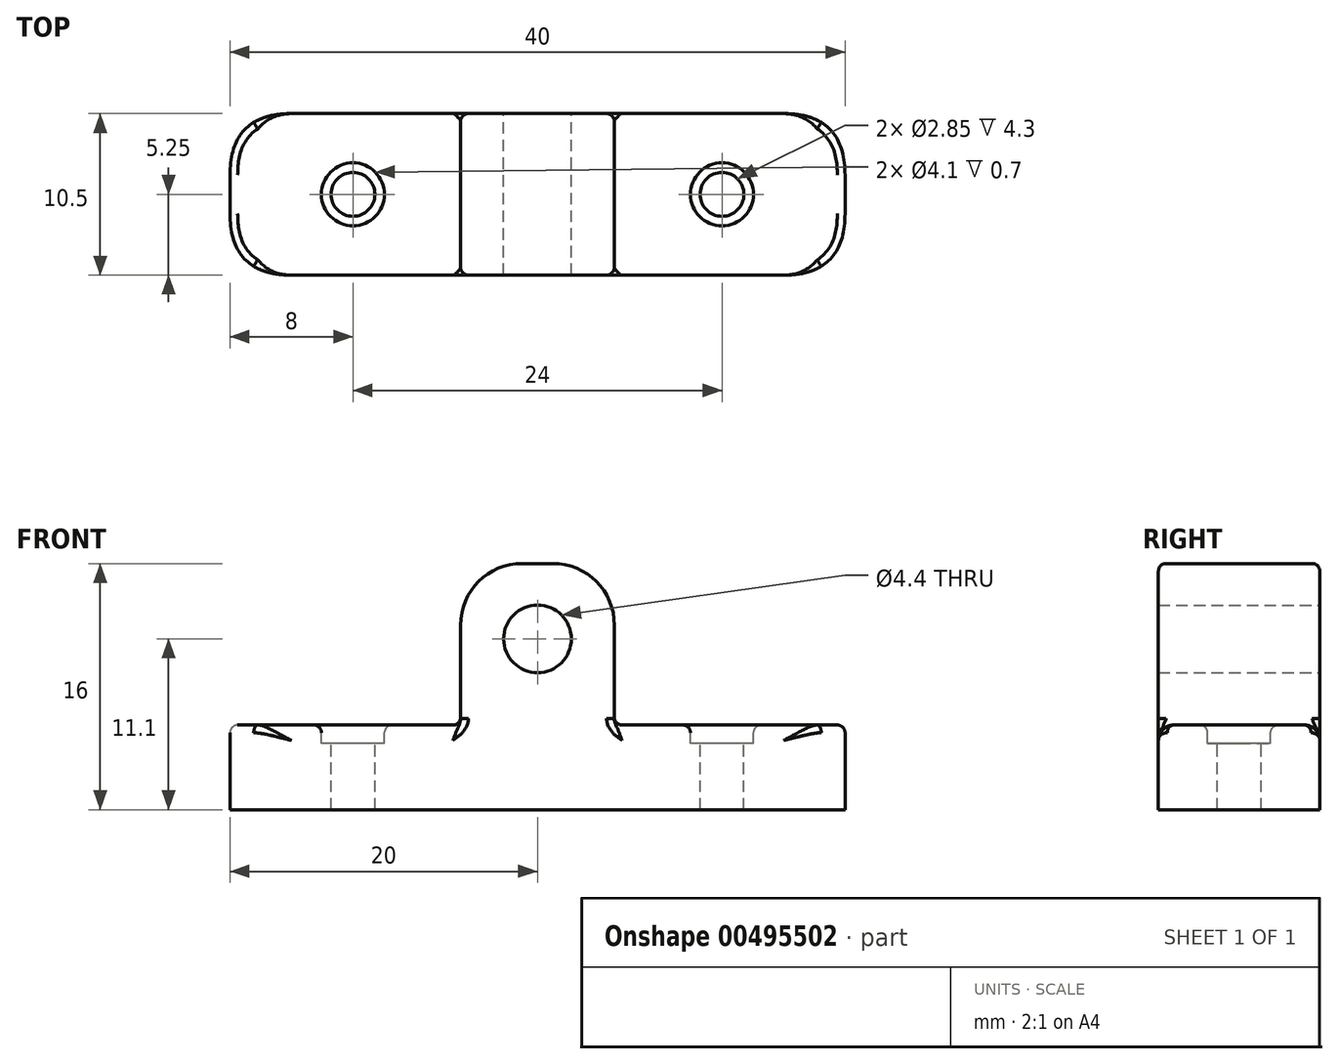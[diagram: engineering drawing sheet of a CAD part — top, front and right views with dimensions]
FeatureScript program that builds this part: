
annotation { "Feature Type Name" : "Feature", "Feature Type Description" : "" }
export const myFeature = defineFeature(function(context is Context, id is Id, definition is map)
    precondition{}
    {
        {
            var Q0;
            Q0=qCreatedBy(makeId("Front.planeOp"),FACE);
            var sketch = newSketch(context, id + "F0", { "sketchPlane" : qUnion([Q0])});
            skLineSegment(sketch, "E0.bottom", {"start": v(-20, 2.75) * mm, "end": v(20, 2.75) * mm});
            skLineSegment(sketch, "E0.top", {"start": v(-20, -2.75) * mm, "end": v(20, -2.75) * mm});
            skLineSegment(sketch, "E0.left", {"start": v(-20, 2.75) * mm, "end": v(-20, -2.75) * mm});
            skLineSegment(sketch, "E0.right", {"start": v(20, 2.75) * mm, "end": v(20, -2.75) * mm});
            skPoint(sketch, "E0.middle", {"position": v(0, 0) * mm});
            skLineSegment(sketch, "E1.top", {"start": v(0, 13.25) * mm, "end": v(5, 13.25) * mm});
            skLineSegment(sketch, "E1.right", {"start": v(5, 2.75) * mm, "end": v(5, 13.25) * mm});
            skLineSegment(sketch, "E2.MirrorCS", {"start": v(0, 13.25) * mm, "end": v(-5, 13.25) * mm});
            skLineSegment(sketch, "E3.MirrorCS", {"start": v(-5, 2.75) * mm, "end": v(-5, 13.25) * mm});
            skCircle(sketch, "E4", {"center": v(0, 8.35) * mm, "radius": 2.2 * mm});
            skSolve(sketch);
        }
        {
            var Q0;
            Q0=makeQuery(id+"F0.imprint","IMPRINT",FACE,{"disambiguationData":[TD([[makeQuery(id+"F0.imprint","IMPRINT",EDGE,{"derivedFrom":sQuery(id+"F0.wireOp",EDGE,"E1.top")}),-1.0]])]});
            var Q1;
            Q1=makeQuery(id+"F0.imprint","IMPRINT",FACE,{"disambiguationData":[TD([[makeQuery(id+"F0.imprint","IMPRINT",EDGE,{"derivedFrom":sQuery(id+"F0.wireOp",EDGE,"E0.top")}),1.0]])]});
            extrude(context, id + "F1", {"entities" : qUnion([Q0, Q1]), "depth" : 10.5 * mm});
        }
        {
            var Q0;
            Q0=makeQuery(id+"F1.opExtrude","SWEPT_EDGE",EDGE,{"disambiguationData":[OSD([sQuery(id+"F0.wireOp",EDGE,"E2.MirrorCS"),sQuery(id+"F0.wireOp",EDGE,"E3.MirrorCS")])]});
            var Q1;
            Q1=makeQuery(id+"F1.opExtrude","SWEPT_EDGE",EDGE,{"disambiguationData":[OSD([sQuery(id+"F0.wireOp",EDGE,"E1.top"),sQuery(id+"F0.wireOp",EDGE,"E1.right")])]});
            fillet(context, id + "F2", {"entities" : qUnion([Q0, Q1]), "radius" : 4 * mm, "tangentPropagation" : true, "allowEdgeOverflow" : false});
        }
        {
            var Q0;
            {var subQ0=sQuery(id+"F0.wireOp",EDGE,"E0.bottom");Q0=makeQuery(id+"F1.opExtrude","SWEPT_FACE",FACE,{"disambiguationData":[OSD([subQ0]),TDD([makeQuery(id+"F0.imprint","IMPRINT",EDGE,{"disambiguationData":[TD([[makeQuery(id+"F0.imprint","INTERSECT",VERTEX,{"derivedFrom":[subQ0,sQuery(id+"F0.wireOp",EDGE,"E0.left")]}),-1.0]])],"derivedFrom":subQ0})])]});}
            var sketch = newSketch(context, id + "F3", { "sketchPlane" : qUnion([Q0])});
            skPoint(sketch, "E5", {"position": v(-12, -5.25) * mm});
            skLineSegment(sketch, "E6", {"start": v(-5, -5.25) * mm, "end": v(-20, -5.25) * mm});
            skPoint(sketch, "E7.MirrorP", {"position": v(12, -5.25) * mm});
            skSolve(sketch);
        }
        {
            var Q0;
            Q0=sQuery(id+"F3.wireOp",VERTEX,"E5");
            var Q1;
            Q1=makeQuery(id+"F1.opExtrude","SWEPT_BODY",BODY,{"disambiguationData":[OSD([sQuery(id+"F0.wireOp",EDGE,"E0.bottom"),sQuery(id+"F0.wireOp",EDGE,"E0.top"),sQuery(id+"F0.wireOp",EDGE,"E0.left"),sQuery(id+"F0.wireOp",EDGE,"E0.right"),sQuery(id+"F0.wireOp",EDGE,"E1.top"),sQuery(id+"F0.wireOp",EDGE,"E1.right"),sQuery(id+"F0.wireOp",EDGE,"E2.MirrorCS"),sQuery(id+"F0.wireOp",EDGE,"E3.MirrorCS"),sQuery(id+"F0.wireOp",EDGE,"E4")])]});
            hole(context, id + "F4", {"style" : HoleStyle.C_BORE, "endStyle" : HoleEndStyle.THROUGH, "holeDiameter" : 2.85 * mm, "cBoreDiameter" : 4.1 * mm, "cBoreDepth" : 1.2 * mm, "isTappedThrough" : true, "tappedDepth" : 12 * mm, "tapClearance" : 3, "locations" : qUnion([Q0]), "scope" : qUnion([Q1])});
        }
        {
            var Q0;
            Q0=sQuery(id+"F3.wireOp",VERTEX,"E7.MirrorP");
            var Q1;
            Q1=makeQuery(id+"F1.opExtrude","SWEPT_BODY",BODY,{"disambiguationData":[OSD([sQuery(id+"F0.wireOp",EDGE,"E0.bottom"),sQuery(id+"F0.wireOp",EDGE,"E0.top"),sQuery(id+"F0.wireOp",EDGE,"E0.left"),sQuery(id+"F0.wireOp",EDGE,"E0.right"),sQuery(id+"F0.wireOp",EDGE,"E1.top"),sQuery(id+"F0.wireOp",EDGE,"E1.right"),sQuery(id+"F0.wireOp",EDGE,"E2.MirrorCS"),sQuery(id+"F0.wireOp",EDGE,"E3.MirrorCS"),sQuery(id+"F0.wireOp",EDGE,"E4")])]});
            hole(context, id + "F5", {"style" : HoleStyle.C_BORE, "endStyle" : HoleEndStyle.THROUGH, "holeDiameter" : 2.85 * mm, "cBoreDiameter" : 4.1 * mm, "cBoreDepth" : 1.2 * mm, "isTappedThrough" : true, "tappedDepth" : 12 * mm, "tapClearance" : 3, "locations" : qUnion([Q0]), "scope" : qUnion([Q1])});
        }
        {
            var Q0;
            {var subQ0=sQuery(id+"F0.wireOp",EDGE,"E0.bottom");Q0=makeQuery(id+"F1.opExtrude","CAP_EDGE",EDGE,{"disambiguationData":[OSD([subQ0]),TDD([makeQuery(id+"F0.imprint","IMPRINT",EDGE,{"disambiguationData":[TD([[makeQuery(id+"F0.imprint","INTERSECT",VERTEX,{"derivedFrom":[subQ0,sQuery(id+"F0.wireOp",EDGE,"E0.right")]}),1.0]])],"derivedFrom":subQ0})])],"isStart":true});}
            var Q1;
            {var subQ0=sQuery(id+"F0.wireOp",EDGE,"E0.bottom");Q1=makeQuery(id+"F1.opExtrude","CAP_EDGE",EDGE,{"disambiguationData":[OSD([subQ0]),TDD([makeQuery(id+"F0.imprint","IMPRINT",EDGE,{"disambiguationData":[TD([[makeQuery(id+"F0.imprint","INTERSECT",VERTEX,{"derivedFrom":[subQ0,sQuery(id+"F0.wireOp",EDGE,"E0.right")]}),1.0]])],"derivedFrom":subQ0})])],"isStart":false});}
            var Q2;
            {var subQ0=sQuery(id+"F0.wireOp",EDGE,"E0.bottom");Q2=makeQuery(id+"F1.opExtrude","CAP_EDGE",EDGE,{"disambiguationData":[OSD([subQ0]),TDD([makeQuery(id+"F0.imprint","IMPRINT",EDGE,{"disambiguationData":[TD([[makeQuery(id+"F0.imprint","INTERSECT",VERTEX,{"derivedFrom":[subQ0,sQuery(id+"F0.wireOp",EDGE,"E0.left")]}),-1.0]])],"derivedFrom":subQ0})])],"isStart":false});}
            var Q3;
            {var subQ0=sQuery(id+"F0.wireOp",EDGE,"E0.bottom");Q3=makeQuery(id+"F1.opExtrude","CAP_EDGE",EDGE,{"disambiguationData":[OSD([subQ0]),TDD([makeQuery(id+"F0.imprint","IMPRINT",EDGE,{"disambiguationData":[TD([[makeQuery(id+"F0.imprint","INTERSECT",VERTEX,{"derivedFrom":[subQ0,sQuery(id+"F0.wireOp",EDGE,"E0.left")]}),-1.0]])],"derivedFrom":subQ0})])],"isStart":true});}
            fillet(context, id + "F6", {"entities" : qUnion([Q0, Q1, Q2, Q3]), "radius" : 1 * mm, "tangentPropagation" : true, "allowEdgeOverflow" : false});
        }
        {
            var Q0;
            Q0=makeQuery(id+"F1.opExtrude","CAP_EDGE",EDGE,{"disambiguationData":[OSD([sQuery(id+"F0.wireOp",EDGE,"E0.right")])],"isStart":false});
            var Q1;
            Q1=makeQuery(id+"F1.opExtrude","CAP_EDGE",EDGE,{"disambiguationData":[OSD([sQuery(id+"F0.wireOp",EDGE,"E0.right")])],"isStart":true});
            fillet(context, id + "F7", {"entities" : qUnion([Q0, Q1]), "radius" : 4 * mm, "rho" : 0.5, "crossSection" : FilletCrossSection.CONIC, "allowEdgeOverflow" : false});
        }
        {
            var Q0;
            Q0=makeQuery(id+"F1.opExtrude","CAP_EDGE",EDGE,{"disambiguationData":[OSD([sQuery(id+"F0.wireOp",EDGE,"E0.left")])],"isStart":false});
            var Q1;
            Q1=makeQuery(id+"F1.opExtrude","CAP_EDGE",EDGE,{"disambiguationData":[OSD([sQuery(id+"F0.wireOp",EDGE,"E0.left")])],"isStart":true});
            fillet(context, id + "F8", {"entities" : qUnion([Q0, Q1]), "radius" : 4 * mm, "rho" : 0.5, "crossSection" : FilletCrossSection.CONIC, "allowEdgeOverflow" : false});
        }
        {
            var Q0;
            {var subQ0=sQuery(id+"F0.wireOp",EDGE,"E0.bottom");Q0=makeQuery(id+"F1.opExtrude","SWEPT_FACE",FACE,{"disambiguationData":[OSD([subQ0]),TDD([makeQuery(id+"F0.imprint","IMPRINT",EDGE,{"disambiguationData":[TD([[makeQuery(id+"F0.imprint","INTERSECT",VERTEX,{"derivedFrom":[subQ0,sQuery(id+"F0.wireOp",EDGE,"E0.right")]}),1.0]])],"derivedFrom":subQ0})])]});}
            fillet(context, id + "F9", {"entities" : qUnion([Q0]), "radius" : .5 * mm, "tangentPropagation" : true, "allowEdgeOverflow" : false});
        }
        {
            var Q0;
            Q0=makeQuery(id+"F1.opExtrude","SWEPT_EDGE",EDGE,{"disambiguationData":[OSD([sQuery(id+"F0.wireOp",EDGE,"E0.bottom"),sQuery(id+"F0.wireOp",EDGE,"E0.left")])]});
            var Q1;
            {var subQ0=sQuery(id+"F0.wireOp",EDGE,"E0.bottom");Q1=makeQuery(id+"F1.opExtrude","SWEPT_FACE",FACE,{"disambiguationData":[OSD([subQ0]),TDD([makeQuery(id+"F0.imprint","IMPRINT",EDGE,{"disambiguationData":[TD([[makeQuery(id+"F0.imprint","INTERSECT",VERTEX,{"derivedFrom":[subQ0,sQuery(id+"F0.wireOp",EDGE,"E0.left")]}),-1.0]])],"derivedFrom":subQ0})])]});}
            fillet(context, id + "F10", {"entities" : qUnion([Q0, Q1]), "radius" : .5 * mm, "tangentPropagation" : true, "allowEdgeOverflow" : false});
        }
        {
            var Q0;
            Q0=makeQuery(id+"F1.opExtrude","CAP_EDGE",EDGE,{"disambiguationData":[OSD([sQuery(id+"F0.wireOp",EDGE,"E3.MirrorCS")])],"isStart":false});
            var Q1;
            {var subQ0=sQuery(id+"F0.wireOp",EDGE,"E3.MirrorCS");var subQ1=sQuery(id+"F0.wireOp",EDGE,"E2.MirrorCS");Q1=makeQuery(id+"F2.opFillet","BLEND_EDGE",EDGE,{"blendedFrom":[makeQuery(id+"F1.opExtrude","SWEPT_EDGE",EDGE,{"disambiguationData":[OSD([subQ1,subQ0])]}),makeQuery(id+"F1.opExtrude","CAP_FACE",FACE,{"disambiguationData":[OSD([sQuery(id+"F0.wireOp",EDGE,"E0.bottom"),sQuery(id+"F0.wireOp",EDGE,"E0.top"),sQuery(id+"F0.wireOp",EDGE,"E0.left"),sQuery(id+"F0.wireOp",EDGE,"E0.right"),sQuery(id+"F0.wireOp",EDGE,"E1.top"),sQuery(id+"F0.wireOp",EDGE,"E1.right"),subQ1,subQ0,sQuery(id+"F0.wireOp",EDGE,"E4")])],"isStart":false})],"blendedInto":[makeQuery(id+"F1.opExtrude","CAP_FACE",FACE,{"disambiguationData":[OSD([sQuery(id+"F0.wireOp",EDGE,"E0.bottom"),sQuery(id+"F0.wireOp",EDGE,"E0.top"),sQuery(id+"F0.wireOp",EDGE,"E0.left"),sQuery(id+"F0.wireOp",EDGE,"E0.right"),sQuery(id+"F0.wireOp",EDGE,"E1.top"),sQuery(id+"F0.wireOp",EDGE,"E1.right"),subQ1,subQ0,sQuery(id+"F0.wireOp",EDGE,"E4")])],"isStart":false})]});}
            var Q2;
            Q2=makeQuery(id+"F1.opExtrude","CAP_EDGE",EDGE,{"disambiguationData":[OSD([sQuery(id+"F0.wireOp",EDGE,"E1.top"),sQuery(id+"F0.wireOp",EDGE,"E2.MirrorCS")])],"isStart":false});
            var Q3;
            {var subQ0=sQuery(id+"F0.wireOp",EDGE,"E1.right");var subQ1=sQuery(id+"F0.wireOp",EDGE,"E1.top");Q3=makeQuery(id+"F2.opFillet","BLEND_EDGE",EDGE,{"blendedFrom":[makeQuery(id+"F1.opExtrude","SWEPT_EDGE",EDGE,{"disambiguationData":[OSD([subQ1,subQ0])]}),makeQuery(id+"F1.opExtrude","CAP_FACE",FACE,{"disambiguationData":[OSD([sQuery(id+"F0.wireOp",EDGE,"E0.bottom"),sQuery(id+"F0.wireOp",EDGE,"E0.top"),sQuery(id+"F0.wireOp",EDGE,"E0.left"),sQuery(id+"F0.wireOp",EDGE,"E0.right"),subQ1,subQ0,sQuery(id+"F0.wireOp",EDGE,"E2.MirrorCS"),sQuery(id+"F0.wireOp",EDGE,"E3.MirrorCS"),sQuery(id+"F0.wireOp",EDGE,"E4")])],"isStart":false})],"blendedInto":[makeQuery(id+"F1.opExtrude","CAP_FACE",FACE,{"disambiguationData":[OSD([sQuery(id+"F0.wireOp",EDGE,"E0.bottom"),sQuery(id+"F0.wireOp",EDGE,"E0.top"),sQuery(id+"F0.wireOp",EDGE,"E0.left"),sQuery(id+"F0.wireOp",EDGE,"E0.right"),subQ1,subQ0,sQuery(id+"F0.wireOp",EDGE,"E2.MirrorCS"),sQuery(id+"F0.wireOp",EDGE,"E3.MirrorCS"),sQuery(id+"F0.wireOp",EDGE,"E4")])],"isStart":false})]});}
            var Q4;
            Q4=makeQuery(id+"F1.opExtrude","CAP_EDGE",EDGE,{"disambiguationData":[OSD([sQuery(id+"F0.wireOp",EDGE,"E1.right")])],"isStart":false});
            fillet(context, id + "F11", {"entities" : qUnion([Q0, Q1, Q2, Q3, Q4]), "radius" : .5 * mm, "tangentPropagation" : true, "allowEdgeOverflow" : false});
        }
        {
            var Q0;
            Q0=makeQuery(id+"F1.opExtrude","CAP_EDGE",EDGE,{"disambiguationData":[OSD([sQuery(id+"F0.wireOp",EDGE,"E1.right")])],"isStart":true});
            var Q1;
            {var subQ0=sQuery(id+"F0.wireOp",EDGE,"E1.right");var subQ1=sQuery(id+"F0.wireOp",EDGE,"E1.top");Q1=makeQuery(id+"F2.opFillet","BLEND_EDGE",EDGE,{"blendedFrom":[makeQuery(id+"F1.opExtrude","SWEPT_EDGE",EDGE,{"disambiguationData":[OSD([subQ1,subQ0])]}),makeQuery(id+"F1.opExtrude","CAP_FACE",FACE,{"disambiguationData":[OSD([sQuery(id+"F0.wireOp",EDGE,"E0.bottom"),sQuery(id+"F0.wireOp",EDGE,"E0.top"),sQuery(id+"F0.wireOp",EDGE,"E0.left"),sQuery(id+"F0.wireOp",EDGE,"E0.right"),subQ1,subQ0,sQuery(id+"F0.wireOp",EDGE,"E2.MirrorCS"),sQuery(id+"F0.wireOp",EDGE,"E3.MirrorCS"),sQuery(id+"F0.wireOp",EDGE,"E4")])],"isStart":true})],"blendedInto":[makeQuery(id+"F1.opExtrude","CAP_FACE",FACE,{"disambiguationData":[OSD([sQuery(id+"F0.wireOp",EDGE,"E0.bottom"),sQuery(id+"F0.wireOp",EDGE,"E0.top"),sQuery(id+"F0.wireOp",EDGE,"E0.left"),sQuery(id+"F0.wireOp",EDGE,"E0.right"),subQ1,subQ0,sQuery(id+"F0.wireOp",EDGE,"E2.MirrorCS"),sQuery(id+"F0.wireOp",EDGE,"E3.MirrorCS"),sQuery(id+"F0.wireOp",EDGE,"E4")])],"isStart":true})]});}
            var Q2;
            Q2=makeQuery(id+"F1.opExtrude","CAP_EDGE",EDGE,{"disambiguationData":[OSD([sQuery(id+"F0.wireOp",EDGE,"E1.top"),sQuery(id+"F0.wireOp",EDGE,"E2.MirrorCS")])],"isStart":true});
            var Q3;
            {var subQ0=sQuery(id+"F0.wireOp",EDGE,"E3.MirrorCS");var subQ1=sQuery(id+"F0.wireOp",EDGE,"E2.MirrorCS");Q3=makeQuery(id+"F2.opFillet","BLEND_EDGE",EDGE,{"blendedFrom":[makeQuery(id+"F1.opExtrude","SWEPT_EDGE",EDGE,{"disambiguationData":[OSD([subQ1,subQ0])]}),makeQuery(id+"F1.opExtrude","CAP_FACE",FACE,{"disambiguationData":[OSD([sQuery(id+"F0.wireOp",EDGE,"E0.bottom"),sQuery(id+"F0.wireOp",EDGE,"E0.top"),sQuery(id+"F0.wireOp",EDGE,"E0.left"),sQuery(id+"F0.wireOp",EDGE,"E0.right"),sQuery(id+"F0.wireOp",EDGE,"E1.top"),sQuery(id+"F0.wireOp",EDGE,"E1.right"),subQ1,subQ0,sQuery(id+"F0.wireOp",EDGE,"E4")])],"isStart":true})],"blendedInto":[makeQuery(id+"F1.opExtrude","CAP_FACE",FACE,{"disambiguationData":[OSD([sQuery(id+"F0.wireOp",EDGE,"E0.bottom"),sQuery(id+"F0.wireOp",EDGE,"E0.top"),sQuery(id+"F0.wireOp",EDGE,"E0.left"),sQuery(id+"F0.wireOp",EDGE,"E0.right"),sQuery(id+"F0.wireOp",EDGE,"E1.top"),sQuery(id+"F0.wireOp",EDGE,"E1.right"),subQ1,subQ0,sQuery(id+"F0.wireOp",EDGE,"E4")])],"isStart":true})]});}
            var Q4;
            Q4=makeQuery(id+"F1.opExtrude","CAP_EDGE",EDGE,{"disambiguationData":[OSD([sQuery(id+"F0.wireOp",EDGE,"E3.MirrorCS")])],"isStart":true});
            fillet(context, id + "F12", {"entities" : qUnion([Q0, Q1, Q2, Q3, Q4]), "radius" : .5 * mm, "tangentPropagation" : true, "allowEdgeOverflow" : false});
        }
    });
